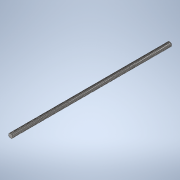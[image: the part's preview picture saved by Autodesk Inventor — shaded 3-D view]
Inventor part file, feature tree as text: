
AUTODESK INVENTOR PART (.ipt)
format: ipt  version: 2020 (Build 240168000, 168)  size: 787,968 bytes
history: native  units: mm
features: sketch x2, extrude x1, helix x1, pattern_circular x1
ambient origin geometry x8: Origin, YZ Plane, XZ Plane, XY Plane, X Axis, Y Axis, Z Axis, Center Point
bodies: Solid1 (feature_tree)
feature tree (5):
  extrude  "Extrusion1"  Depth=8.0mm TaperAngle=0.0deg
  helix  "Coil1"  [1 undecoded]
  pattern_circular  "Circular Pattern1"  Count=4 Angle=360.0deg
  sketch  "Sketch1"  dims[d0=8.0mm d1=300.0mm d2=0.0mm d3=1.0mm]
  sketch  "Sketch2"  dims[d4=3.8mm d5=8.0mm d6=10.0mm d7=437.5mm d8=0.0mm d9=90.0deg d10=90.0deg d11=0.0mm d12=0.0mm d13=40.0mm d14=360.0deg]
note: 1 required parameter value undecoded (feature->parameter linkage not recoverable at this tier; creation-order binding heuristic only, values carry confidence <= 0.55)
